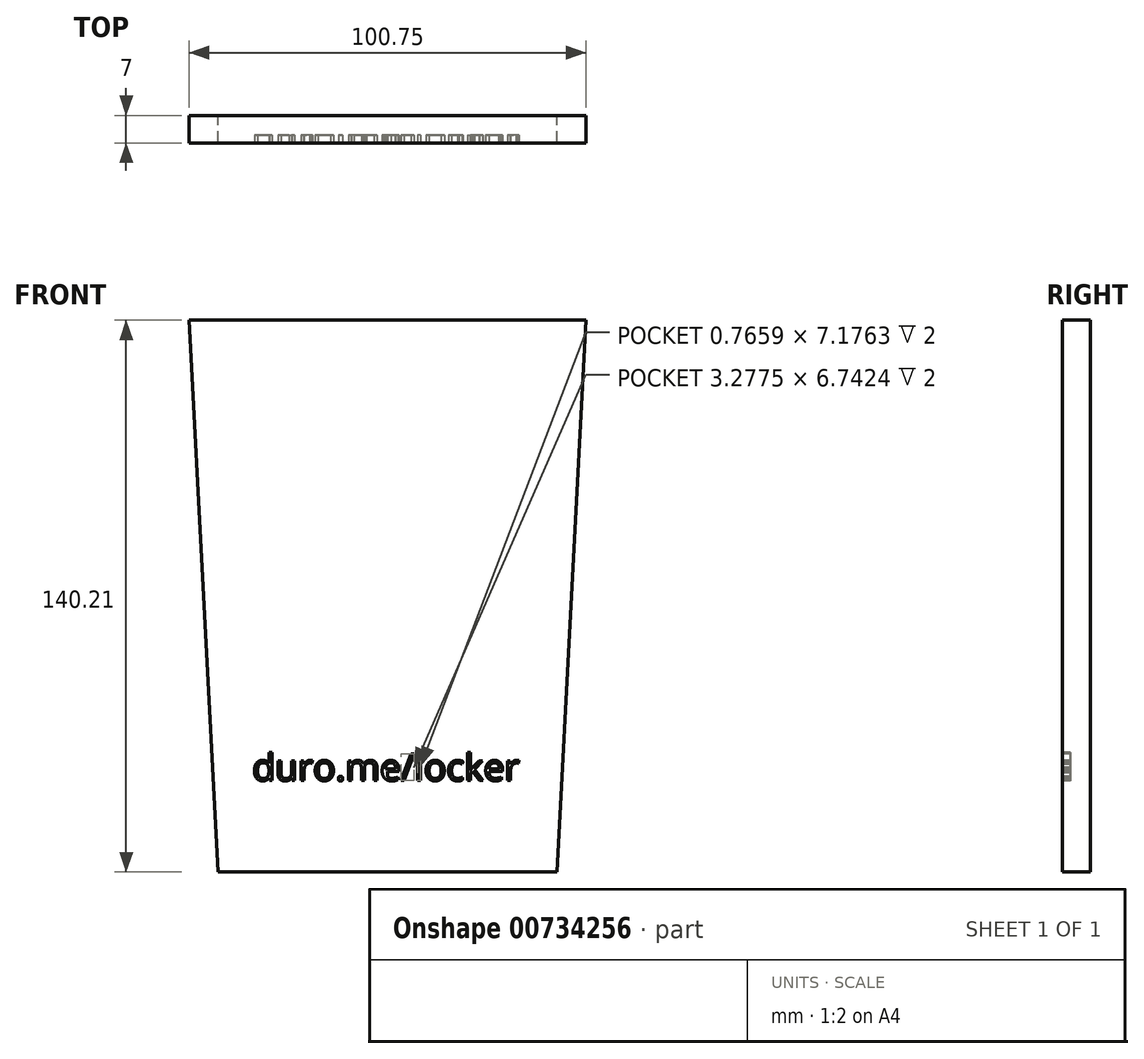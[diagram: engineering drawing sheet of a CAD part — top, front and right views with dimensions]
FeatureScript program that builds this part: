
annotation { "Feature Type Name" : "Feature", "Feature Type Description" : "" }
export const myFeature = defineFeature(function(context is Context, id is Id, definition is map)
    precondition{}
    {
        {
            var Q0;
            Q0=qCreatedBy(makeId("Front.planeOp"),FACE);
            var sketch = newSketch(context, id + "F0", { "sketchPlane" : qUnion([Q0])});
            skLineSegment(sketch, "E0", {"start": v(-39.9, 49.12) * mm, "end": v(60.86, 49.12) * mm});
            skLineSegment(sketch, "E1", {"start": v(60.86, 49.12) * mm, "end": v(53.51, -91.09) * mm});
            skLineSegment(sketch, "E2", {"start": v(53.51, -91.09) * mm, "end": v(-32.55, -91.09) * mm});
            skLineSegment(sketch, "E3", {"start": v(-32.55, -91.09) * mm, "end": v(-39.9, 49.12) * mm});
            skSolve(sketch);
        }
        {
            var Q0;
            Q0=makeQuery(id+"F0.imprint","IMPRINT",FACE,{"disambiguationData":[TD([[makeQuery(id+"F0.imprint","IMPRINT",EDGE,{"derivedFrom":sQuery(id+"F0.wireOp",EDGE,"E0")}),-1.0]])]});
            extrude(context, id + "F1", {"entities" : qUnion([Q0]), "depth" : 7 * mm, "offsetDistance" : 25 * mm});
        }
        {
            var Q0;
            Q0=makeQuery(id+"F1.opExtrude","CAP_FACE",FACE,{"disambiguationData":[OSD([sQuery(id+"F0.wireOp",EDGE,"E0"),sQuery(id+"F0.wireOp",EDGE,"E1"),sQuery(id+"F0.wireOp",EDGE,"E2"),sQuery(id+"F0.wireOp",EDGE,"E3")])],"isStart":false});
            var sketch = newSketch(context, id + "F2", { "sketchPlane" : qUnion([Q0])});
            skText(sketch, "E4", { "text": "duro.me/locker", "fontName": "OpenSans-Regular.ttf"});
            skLineSegment(sketch, "E5", {"start": v(10.48, 49.12) * mm, "end": v(10.48, -91.09) * mm});
            const initialGuessF2  = {"E4": [-0.02387, -0.06786, 1, 0, 0.0068]};
            skSetInitialGuess(sketch, initialGuessF2);
            skSolve(sketch);
        }
        {
            var Q0;
            Q0 = qSketchRegion(id + "F2", true);
            extrude(context, id + "F3", {"entities" : qUnion([Q0]), "operationType" : NewBodyOperationType.REMOVE, "oppositeDirection" : true, "depth" : 2 * mm, "offsetDistance" : 25 * mm});
        }
    });
